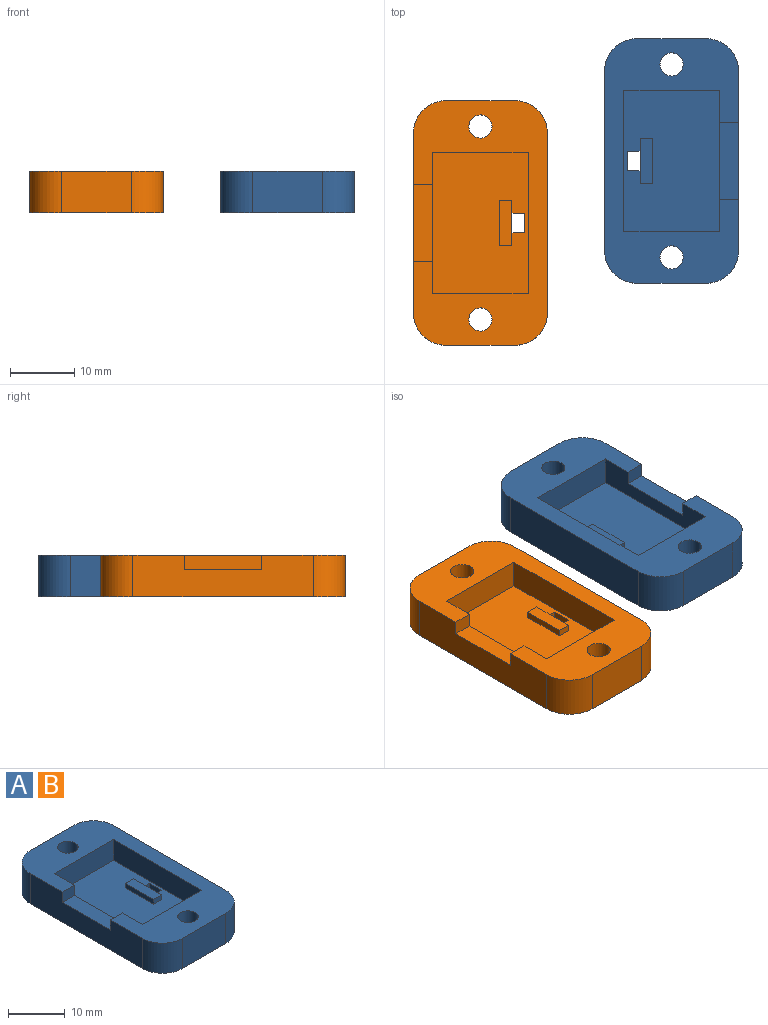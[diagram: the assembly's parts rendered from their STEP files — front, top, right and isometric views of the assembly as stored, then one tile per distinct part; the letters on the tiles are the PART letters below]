
ASSEMBLY  parts=2 mates=1
PART A: 28 faces, bbox 20.8x38x6.5 mm
  f0: plane 10.8x6.5mm, normal (0,1,0), area 70.2mm2, adj f12,f13,f24,f27
  f1: plane 3x2.2mm, normal (0,-1,0), area 6.6mm2, adj f5,f7,f12,f23
  f2: plane 14.8x4.5mm, normal (0,-1,0), area 66.6mm2, adj f3,f5,f12,f17
  f3: plane 22x4.5mm, normal (-1,0,0), area 99mm2, adj f2,f4,f12,f17
  f4: plane 14.8x4.5mm, normal (0,1,0), area 66.6mm2, adj f3,f5,f12,f17
  f5: plane 22x4.5mm, normal (1,0,0), area 72.6mm2, adj f1,f2,f4,f6,f12,f17,f23
  f6: plane 3x2.2mm, normal (0,1,0), area 6.6mm2, adj f5,f7,f12,f23
  f7: plane 28x6.5mm, normal (-1,0,0), area 155.6mm2, adj f1,f6,f12,f13,f23,f24,f25
  f8: plane 10.8x6.5mm, normal (0,-1,0), area 70.2mm2, adj f12,f13,f25,f26
  f9: cylinder r=1.8mm len=6.5mm, axis (0,0,-1), area 73.5mm2, adj f12,f13
  f10: cylinder r=1.8mm len=6.5mm, axis (0,0,-1), area 73.5mm2, adj f12,f13
  f11: plane 28x6.5mm, normal (1,0,0), area 182mm2, adj f12,f13,f26,f27
  f12: plane 38x20.8mm, normal (0,0,1), area 387mm2, adj f0,f1,f2,f3,f4,f5,f6,f7
  f13: plane 38x20.8mm, normal (0,0,-1), area 742.6mm2, adj f0,f7,f8,f9,f10,f11,f14,f15
  f14: plane 2x2mm, normal (0,1,0), area 4mm2, adj f13,f16,f17,f18
  f15: plane 2x2mm, normal (0,-1,0), area 4mm2, adj f13,f16,f17,f18
  f16: plane 3x2mm, normal (-1,0,0), area 6mm2, adj f13,f14,f15,f17
  f17: plane 22x14.8mm, normal (0,0,1), area 305.6mm2, adj f2,f3,f4,f5,f14,f15,f16,f18
  f18: plane 7x3mm, normal (1,0,0), area 13mm2, adj f13,f14,f15,f17,f19,f21,f22
  f19: plane 2x1mm, normal (0,1,0), area 2mm2, adj f17,f18,f20,f22
  f20: plane 7x1mm, normal (-1,0,0), area 7mm2, adj f17,f19,f21,f22
  f21: plane 2x1mm, normal (0,-1,0), area 2mm2, adj f17,f18,f20,f22
  f22: plane 7x2mm, normal (0,0,1), area 14mm2, adj f18,f19,f20,f21
  f23: plane 12x3mm, normal (0,0,1), area 36mm2, adj f1,f5,f6,f7
  f24: cylinder r=5mm len=6.5mm, axis (0,0,1), area 51.1mm2, adj f0,f7,f12,f13
  f25: cylinder r=5mm len=6.5mm, axis (0,0,-1), area 51.1mm2, adj f7,f8,f12,f13
  f26: cylinder r=5mm len=6.5mm, axis (0,0,1), area 51.1mm2, adj f8,f11,f12,f13
  f27: cylinder r=5mm len=6.5mm, axis (0,0,-1), area 51.1mm2, adj f0,f11,f12,f13
PART B: same geometry as A
PLACE A rot(axis=(0,0,1),180deg) t=(19.95,12.62,3.19)mm
PLACE B t=(-9.76,2.98,3.19)mm
MATE planar B.f13 <-> A.f13  axis (0,0,-1) through (-9.81,2.98,3.19)mm
